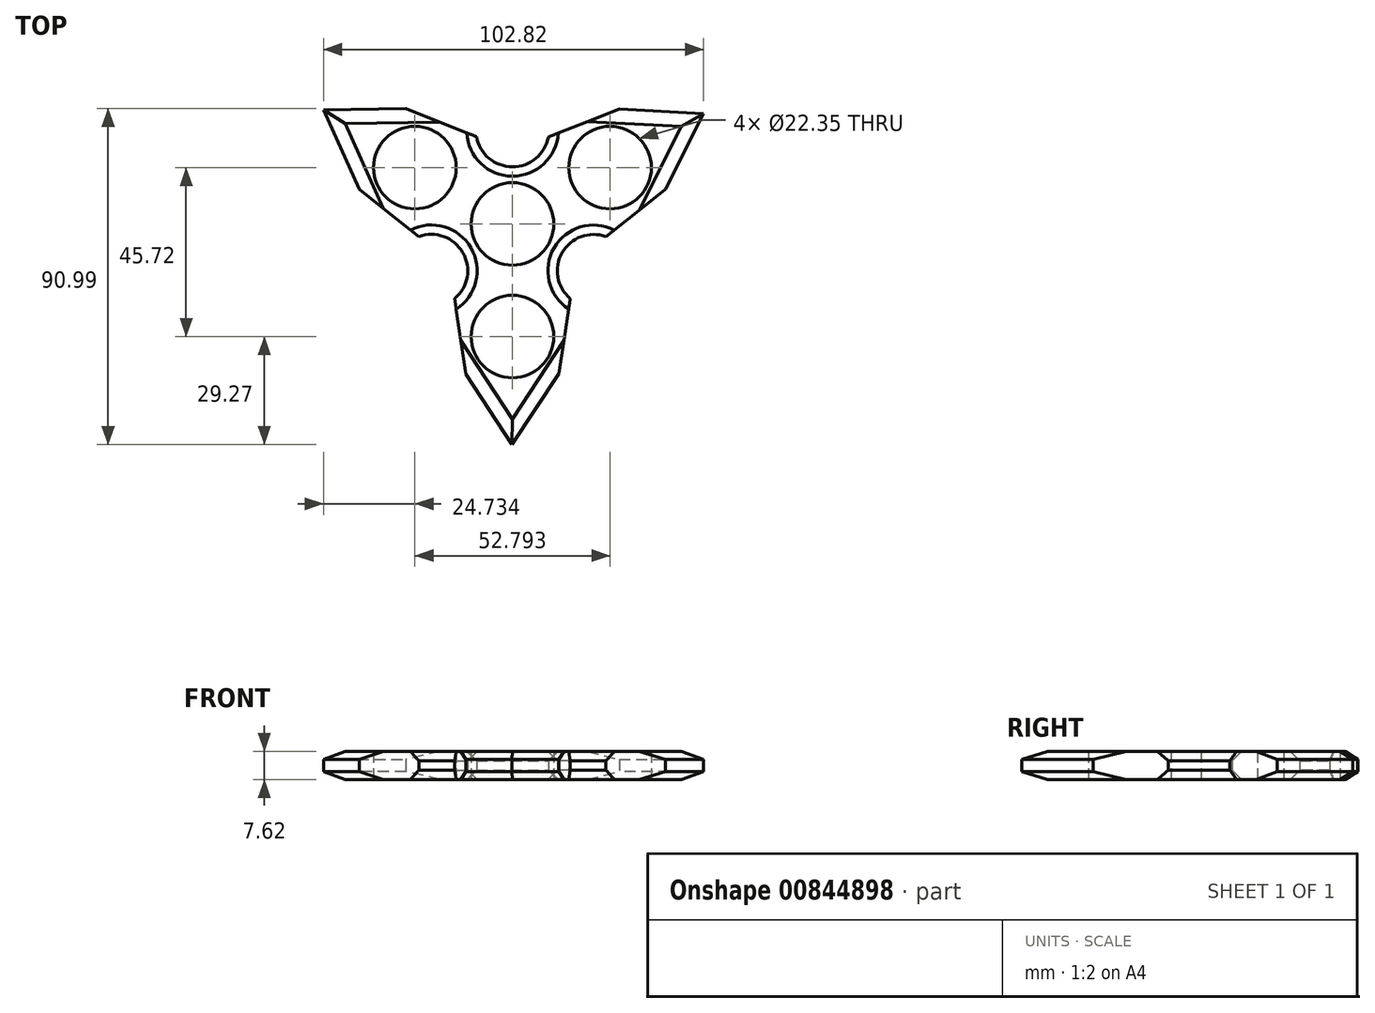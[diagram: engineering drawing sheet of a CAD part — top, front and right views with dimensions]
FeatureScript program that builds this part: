
annotation { "Feature Type Name" : "Feature", "Feature Type Description" : "" }
export const myFeature = defineFeature(function(context is Context, id is Id, definition is map)
    precondition{}
    {
        {
            var Q0;
            Q0=qCreatedBy(makeId("Top.planeOp"),FACE);
            var sketch = newSketch(context, id + "F0", { "sketchPlane" : qUnion([Q0])});
            skPoint(sketch, "E0.center", {"position": v(0, 0) * mm});
            skCircle(sketch, "E1", {"center": v(-26.4, 15.24) * mm, "radius": 11.18 * mm});
            skCircle(sketch, "E2", {"center": v(0, 0) * mm, "radius": 11.18 * mm});
            skCircle(sketch, "E3.1.0", {"center": v(0, -30.48) * mm, "radius": 11.18 * mm});
            skCircle(sketch, "E3.2.0", {"center": v(26.4, 15.24) * mm, "radius": 11.18 * mm});
            skPoint(sketch, "E4.middle", {"position": v(0, -15.24) * mm});
            skLineSegment(sketch, "E5", {"start": v(-9.7, 23.6) * mm, "end": v(-19.39, 27.47) * mm});
            skLineSegment(sketch, "E6.1.0", {"start": v(-25.34, -3.42) * mm, "end": v(-33.5, 3.08) * mm});
            skLineSegment(sketch, "E6.1.1", {"start": v(-15.63, -20.23) * mm, "end": v(-14.08, -30.54) * mm});
            skLineSegment(sketch, "E6.2.0", {"start": v(15.64, -20.19) * mm, "end": v(14.1, -30.45) * mm});
            skLineSegment(sketch, "E7", {"start": v(-33.5, 3.08) * mm, "end": v(-41.44, 9.41) * mm});
            skLineSegment(sketch, "E8", {"start": v(-19.39, 27.47) * mm, "end": v(-28.82, 31.24) * mm});
            skLineSegment(sketch, "E9", {"start": v(14.1, -30.45) * mm, "end": v(12.58, -40.5) * mm});
            skLineSegment(sketch, "E10", {"start": v(-14.08, -30.54) * mm, "end": v(-12.57, -40.6) * mm});
            skLineSegment(sketch, "E11", {"start": v(9.7, 23.53) * mm, "end": v(28.87, 31.05) * mm});
            skLineSegment(sketch, "E12", {"start": v(19.41, 27.34) * mm, "end": v(28.87, 31.05) * mm});
            skLineSegment(sketch, "E13.trimOffspring", {"start": v(25.3, -3.45) * mm, "end": v(41.36, 9.35) * mm});
            skPoint(sketch, "E14.start.orphan", {"position": v(0, -44.45) * mm});
            skLineSegment(sketch, "E15", {"start": v(-51.13, 30.88) * mm, "end": v(-41.44, 9.41) * mm});
            skLineSegment(sketch, "E16", {"start": v(-51.13, 30.88) * mm, "end": v(-28.82, 31.24) * mm});
            skLineSegment(sketch, "E17", {"start": v(-0.1, -59.75) * mm, "end": v(-12.57, -40.6) * mm});
            skLineSegment(sketch, "E18", {"start": v(-0.1, -59.75) * mm, "end": v(12.58, -40.5) * mm});
            skLineSegment(sketch, "E19", {"start": v(51.7, 29.84) * mm, "end": v(41.36, 9.35) * mm});
            skLineSegment(sketch, "E20", {"start": v(51.7, 29.84) * mm, "end": v(28.87, 31.05) * mm});
            skArc(sketch, "E21", {"start": v(-15.63, -20.23) * mm, "mid": v(-13.43, -7.76) * mm, "end": v(-25.34, -3.42) * mm});
            skLineSegment(sketch, "E22", {"start": v(19.41, 27.34) * mm, "end": v(9.7, 23.53) * mm});
            skArc(sketch, "E23", {"start": v(-9.7, 23.6) * mm, "mid": v(-0.02, 15.45) * mm, "end": v(9.7, 23.53) * mm});
            skLineSegment(sketch, "E24", {"start": v(41.36, 9.35) * mm, "end": v(33.42, 3.02) * mm});
            skArc(sketch, "E25", {"start": v(25.3, -3.45) * mm, "mid": v(13.43, -7.76) * mm, "end": v(15.64, -20.19) * mm});
            skPoint(sketch, "E26.end.orphan", {"position": v(17.76, 0) * mm});
            skPoint(sketch, "E26.start.orphan", {"position": v(13.43, -7.76) * mm});
            skPoint(sketch, "E27.orphan", {"position": v(-17.19, -9.92) * mm});
            skPoint(sketch, "E28.orphan", {"position": v(0, 19.72) * mm});
            skPoint(sketch, "E29.start.orphan", {"position": v(0.08, 11.18) * mm});
            skPoint(sketch, "E30.orphan", {"position": v(17.19, -9.92) * mm});
            skPoint(sketch, "E31.start.orphan", {"position": v(0.04, 15.45) * mm});
            skPoint(sketch, "E32.end.orphan", {"position": v(-9.68, -5.59) * mm});
            skPoint(sketch, "E32.start.orphan", {"position": v(-13.43, -7.76) * mm});
            skPoint(sketch, "E33.start.orphan", {"position": v(9.68, -5.59) * mm});
            skSolve(sketch);
        }
        {
            var Q0;
            Q0=qSketchRegion(id+"F0",true);
            var Q1;
            {var subQ1=sQuery(id+"F0.wireOp",EDGE,"VKsS3Otb-miZj-gkGU-12GB-d8zIMCj1J9sK");var subQ7=makeQuery(id+"F0.imprint","INTERSECT",VERTEX,{"derivedFrom":[subQ1,sQuery(id+"F0.wireOp",EDGE,"2a81f7ea-dfaa-4220-9730-6b88422f781c.2.0")]});Q1=makeQuery(id+"F0.imprint","IMPRINT",FACE,{"disambiguationData":[TD([[makeQuery(id+"F0.imprint","IMPRINT",EDGE,{"disambiguationData":[TD([[subQ7,-1.0]])],"derivedFrom":subQ1}),1.0]])]});}
            var Q2;
            {var subQ3=sQuery(id+"F0.wireOp",EDGE,"2b8rqVyu-uKhq-1D1T-Kwuw-1NqnRaVyucTM");var subQ5=sQuery(id+"F0.wireOp",EDGE,"E2");var subQ6=makeQuery(id+"F0.imprint","INTERSECT",VERTEX,{"derivedFrom":[subQ5,subQ3]});Q2=makeQuery(id+"F0.imprint","IMPRINT",FACE,{"disambiguationData":[TD([[makeQuery(id+"F0.imprint","IMPRINT",EDGE,{"disambiguationData":[TD([[subQ6,-1.0]])],"derivedFrom":subQ5}),-1.0]])]});}
            var Q3;
            {var subQ5=sQuery(id+"F0.wireOp",EDGE,"VKsS3Otb-miZj-gkGU-12GB-d8zIMCj1J9sK");var subQ8=makeQuery(id+"F0.imprint","INTERSECT",VERTEX,{"derivedFrom":[subQ5,sQuery(id+"F0.wireOp",EDGE,"ad422b94-503c-4b8c-a564-e47813131238.2.1")]});Q3=makeQuery(id+"F0.imprint","IMPRINT",FACE,{"disambiguationData":[TD([[makeQuery(id+"F0.imprint","IMPRINT",EDGE,{"disambiguationData":[TD([[subQ8,1.0]])],"derivedFrom":subQ5}),1.0]])]});}
            var Q4;
            {var subQ3=sQuery(id+"F0.wireOp",EDGE,"KG0W6A2v-qbmV-kile-noT2-Lh5GOKsosSiX");var subQ5=sQuery(id+"F0.wireOp",EDGE,"E2");var subQ6=makeQuery(id+"F0.imprint","INTERSECT",VERTEX,{"derivedFrom":[subQ5,subQ3]});Q4=makeQuery(id+"F0.imprint","IMPRINT",FACE,{"disambiguationData":[TD([[makeQuery(id+"F0.imprint","IMPRINT",EDGE,{"disambiguationData":[TD([[subQ6,1.0]])],"derivedFrom":subQ5}),-1.0]])]});}
            var Q5;
            {var subQ1=sQuery(id+"F0.wireOp",EDGE,"VKsS3Otb-miZj-gkGU-12GB-d8zIMCj1J9sK");var subQ7=makeQuery(id+"F0.imprint","INTERSECT",VERTEX,{"derivedFrom":[subQ1,sQuery(id+"F0.wireOp",EDGE,"ad422b94-503c-4b8c-a564-e47813131238.1.1")]});Q5=makeQuery(id+"F0.imprint","IMPRINT",FACE,{"disambiguationData":[TD([[makeQuery(id+"F0.imprint","IMPRINT",EDGE,{"disambiguationData":[TD([[subQ7,1.0]])],"derivedFrom":subQ1}),1.0]])]});}
            extrude(context, id + "F1", {"entities" : qUnion([Q0, Q1, Q2, Q3, Q4, Q5]), "depth" : 7.62 * mm, "offsetDistance" : 25.4 * mm});
        }
        {
            var Q0;
            Q0=makeQuery(id+"F1.opExtrude","CAP_EDGE",EDGE,{"disambiguationData":[OSD([sQuery(id+"F0.wireOp",EDGE,"E15")])],"isStart":false});
            var Q1;
            Q1=makeQuery(id+"F1.opExtrude","CAP_EDGE",EDGE,{"disambiguationData":[OSD([sQuery(id+"F0.wireOp",EDGE,"E19")])],"isStart":true});
            var Q2;
            Q2=makeQuery(id+"F1.opExtrude","CAP_EDGE",EDGE,{"disambiguationData":[OSD([sQuery(id+"F0.wireOp",EDGE,"E16")])],"isStart":true});
            var Q3;
            Q3=makeQuery(id+"F1.opExtrude","CAP_EDGE",EDGE,{"disambiguationData":[OSD([sQuery(id+"F0.wireOp",EDGE,"E15")])],"isStart":true});
            var Q4;
            Q4=makeQuery(id+"F1.opExtrude","CAP_EDGE",EDGE,{"disambiguationData":[OSD([sQuery(id+"F0.wireOp",EDGE,"E16")])],"isStart":false});
            var Q5;
            Q5=makeQuery(id+"F1.opExtrude","CAP_EDGE",EDGE,{"disambiguationData":[OSD([sQuery(id+"F0.wireOp",EDGE,"E20")])],"isStart":false});
            var Q6;
            Q6=makeQuery(id+"F1.opExtrude","CAP_EDGE",EDGE,{"disambiguationData":[OSD([sQuery(id+"F0.wireOp",EDGE,"E19")])],"isStart":false});
            var Q7;
            Q7=makeQuery(id+"F1.opExtrude","CAP_EDGE",EDGE,{"disambiguationData":[OSD([sQuery(id+"F0.wireOp",EDGE,"E18")])],"isStart":false});
            var Q8;
            Q8=makeQuery(id+"F1.opExtrude","CAP_EDGE",EDGE,{"disambiguationData":[OSD([sQuery(id+"F0.wireOp",EDGE,"E17")])],"isStart":false});
            chamfer(context, id + "F2", {"entities" : qUnion([Q0, Q1, Q2, Q3, Q4, Q5, Q6, Q7, Q8]), "chamferType" : ChamferType.OFFSET_ANGLE, "width" : 3.8 * mm, "oppositeDirection" : false, "angle" : 30 * degree, "tangentPropagation" : true});
        }
        {
            var Q0;
            Q0=makeQuery(id+"F1.opExtrude","CAP_EDGE",EDGE,{"disambiguationData":[OSD([sQuery(id+"F0.wireOp",EDGE,"E17")])],"isStart":true});
            var Q1;
            Q1=makeQuery(id+"F1.opExtrude","CAP_EDGE",EDGE,{"disambiguationData":[OSD([sQuery(id+"F0.wireOp",EDGE,"E18")])],"isStart":true});
            var Q2;
            Q2=makeQuery(id+"F1.opExtrude","CAP_EDGE",EDGE,{"disambiguationData":[OSD([sQuery(id+"F0.wireOp",EDGE,"E20")])],"isStart":true});
            chamfer(context, id + "F3", {"entities" : qUnion([Q0, Q1, Q2]), "chamferType" : ChamferType.OFFSET_ANGLE, "width" : 3.8 * mm, "oppositeDirection" : false, "angle" : 30 * degree, "tangentPropagation" : true});
        }
        {
            var Q0;
            Q0=makeQuery(id+"F1.opExtrude","CAP_EDGE",EDGE,{"disambiguationData":[OSD([sQuery(id+"F0.wireOp",EDGE,"E23")])],"isStart":false});
            var Q1;
            Q1=makeQuery(id+"F1.opExtrude","CAP_EDGE",EDGE,{"disambiguationData":[OSD([sQuery(id+"F0.wireOp",EDGE,"E25")])],"isStart":false});
            var Q2;
            Q2=makeQuery(id+"F1.opExtrude","CAP_EDGE",EDGE,{"disambiguationData":[OSD([sQuery(id+"F0.wireOp",EDGE,"E21")])],"isStart":false});
            var Q3;
            Q3=makeQuery(id+"F1.opExtrude","CAP_EDGE",EDGE,{"disambiguationData":[OSD([sQuery(id+"F0.wireOp",EDGE,"E21")])],"isStart":true});
            var Q4;
            Q4=makeQuery(id+"F1.opExtrude","CAP_EDGE",EDGE,{"disambiguationData":[OSD([sQuery(id+"F0.wireOp",EDGE,"E23")])],"isStart":true});
            var Q5;
            Q5=makeQuery(id+"F1.opExtrude","CAP_EDGE",EDGE,{"disambiguationData":[OSD([sQuery(id+"F0.wireOp",EDGE,"E25")])],"isStart":true});
            chamfer(context, id + "F4", {"entities" : qUnion([Q0, Q1, Q2, Q3, Q4, Q5]), "width" : 2.54 * mm, "tangentPropagation" : true});
        }
    });
